# Revit family: PRD_AR_FlshCntrlDvcs_ElectronicTrapControl_AQUA422N 2
name_source: partatom
category: Specialty Equipment
units: mm (PartAtom-declared; Revit-internal decimal feet)

## family parameters
Always vertical = Yes
Cut with Voids When Loaded = No
Enable Cutting in Views = No
Maintain Annotation Orientation = No
OmniClass Number = 23.45.55.11
OmniClass Title = Sanitary Components
Part Type = Normal
Room Calculation Point = No
Round Connector Dimension = Use Diameter
Shared = No
Work Plane-Based = No

## types (1)
- AQUA422N
    ApparentLoad = 0 VA
    AssetType = Fixed
    BIMObjectName = PRD_AR_FlushControlDevices_ElectronicTrapControl_AQUA422N
    BasicColour = other
    BodyMaterial = PRD_AR_Plastic_White
    Category = Pr_75_50_46_31, Flush control devices
    CloseOffRating = 0.0 Pa
    Default Elevation = 0 mm  [stored 0 ft]
    DefaultAutomaticHygieneFlushing = 24h after the last activity
    Description = Electronic siphon control unit for invisible installation, for touch-free flushing of KWC stainless steel trough urinals. With connection hoses, solenoid valve, siphon with externally mounted sensor without water contact and electronic box including power supply unit and control with extended blocking time, 230 V AC. Trap cover must be ordered separately.
    DiameterNominal = DN 15
    Export Type to IFC As = IfcValveType
    Features = With connection hoses, solenoid valve, siphon with externally mounted sensor and electronic box.
    FlowCoefficient = 0
    FlowOutlet = 0.0 L/s
    FlushingRate = 0.0 L/s
    FlushingVolumeAdjustable = no
    FunctionalPrinciple = electronic self-closing
    HasIntegralShutOffDevice = Yes
    IfcExportAs = IfcValve
    IfcExportType = FLUSHING
    InletConversionSize = 40 mm
    InletSize = G 1/2 B
    IsHighPressure = No
    Manufacturer = KWC Group Management AG
    ManufacturerName = KWC Group Management AG
    ManufacturerURL = www.kwc-professional.com
    MaterialFitting = synthetic
    MinimumFlowPressure = 1 bar
    Model = AQUA422N
    ModelNumber = 3600002630
    ModelReference = AQUA422N
    NBSDescription = Flush control devices
    NBSReference = 90-15-35/470
    Name = Electronic trap control AQUA422N
    NominalDepth = 0 mm  [stored 0 ft]
    NominalHeight = 0 mm  [stored 0 ft]
    NominalWidth = 0 mm  [stored 0 ft]
    OutletSize = 40 mm
    Parameterization = manual
    PowerSupplyConnection = 230 V AC
    ProductInformation = http://pim.kwc.com
    ProtectiveSystemIp = IP68
    Size = 15 mm  [stored 0.0492126 ft]
    SoundInsulation = no
    Status = New
    TestPressure = 0.0 Pa
    Type IFC Predefined Type = FLUSHING
    TypeOfFlushingFitting = urinal flush valve
    TypeOfMounting = wall mounting
    TypeOfOperation = sensor operation
    TypeOfPowerSupply = Transformer
    TypeOfSensor = radar-electronic sensor
    URL = www.kwc-professional.com
    Uniclass2015Code = Pr_75_50_46_31
    Uniclass2015Title = Flush control devices
    Uniclass2015Version = Products v1.38
    ValveMechanism = OTHER
    ValveOperation = SOLENOID
    ValvePattern = STRAIGHT_2_PORT
    Version = 1
    Voltage = 230 V
    WaterConnection = threaded connection (external)
    WithTransformer/PowerSupply = yes
    WorkingPressure = 0.0 Pa

note: [stored X ft] marks values corroborated as IEEE doubles in the binary element streams (Revit-internal decimal feet)

## geometry (parser evidence)
native form markers: Sweep x2
no freeform markers — native parametric forms only
